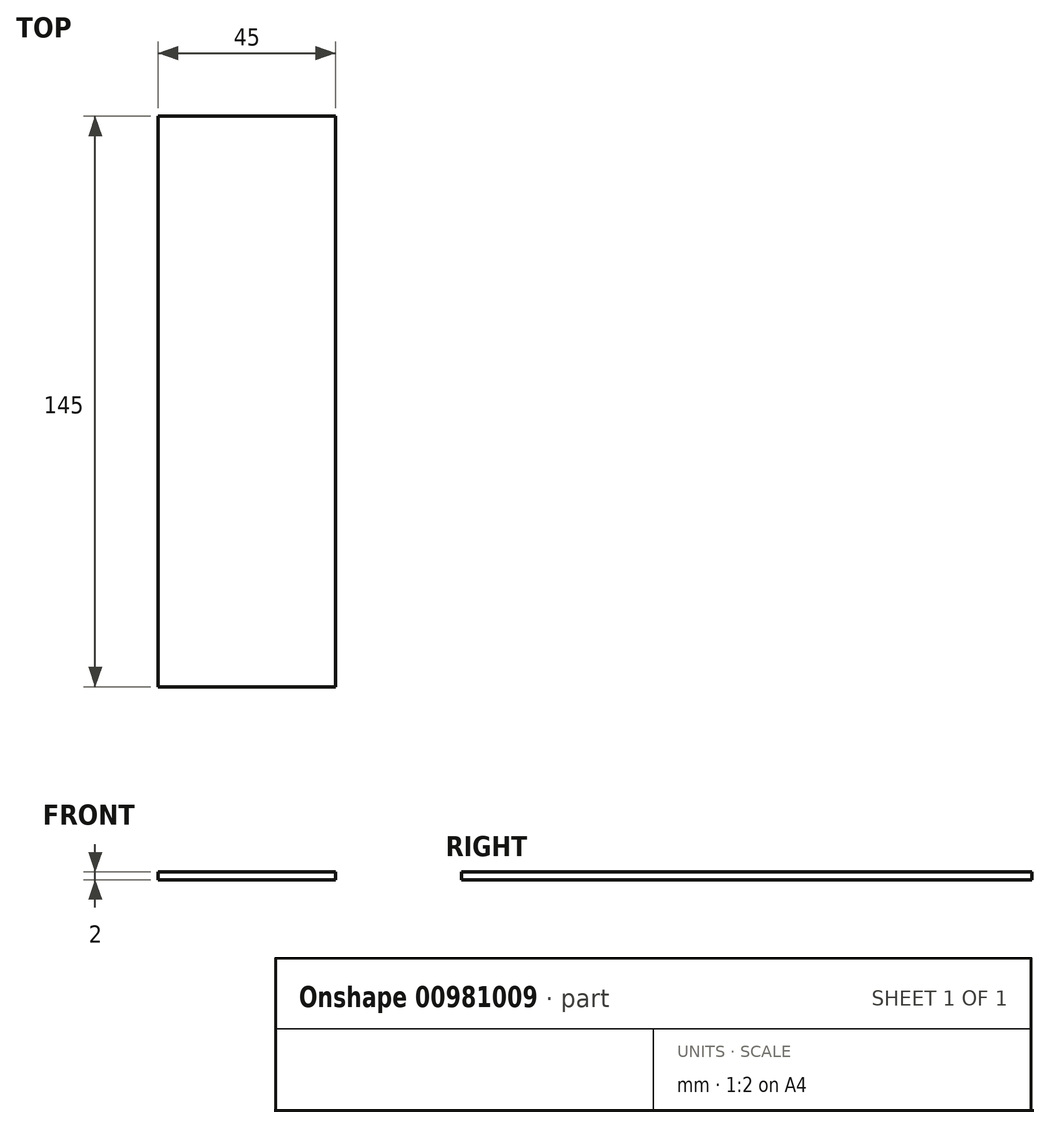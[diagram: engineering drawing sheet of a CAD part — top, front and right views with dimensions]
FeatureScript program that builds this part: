
annotation { "Feature Type Name" : "Feature", "Feature Type Description" : "" }
export const myFeature = defineFeature(function(context is Context, id is Id, definition is map)
    precondition{}
    {
        {
            var Q0;
            Q0=qCreatedBy(makeId("Top.planeOp"),FACE);
            var sketch = newSketch(context, id + "F0", { "sketchPlane" : qUnion([Q0])});
            skLineSegment(sketch, "E0.bottom", {"start": v(22.5, 72.5) * mm, "end": v(-22.5, 72.5) * mm});
            skLineSegment(sketch, "E0.top", {"start": v(22.5, -72.5) * mm, "end": v(-22.5, -72.5) * mm});
            skLineSegment(sketch, "E0.left", {"start": v(22.5, 72.5) * mm, "end": v(22.5, -72.5) * mm});
            skLineSegment(sketch, "E0.right", {"start": v(-22.5, 72.5) * mm, "end": v(-22.5, -72.5) * mm});
            skPoint(sketch, "E0.middle", {"position": v(0, 0) * mm});
            skSolve(sketch);
        }
        {
            var Q0;
            Q0=makeQuery(id+"F0.imprint","IMPRINT",FACE,{"disambiguationData":[TD([[makeQuery(id+"F0.imprint","IMPRINT",EDGE,{"derivedFrom":sQuery(id+"F0.wireOp",EDGE,"E0.bottom")}),1.0]])]});
            extrude(context, id + "F1", {"entities" : qUnion([Q0]), "depth" : 2 * mm, "offsetDistance" : 25 * mm});
        }
    });
